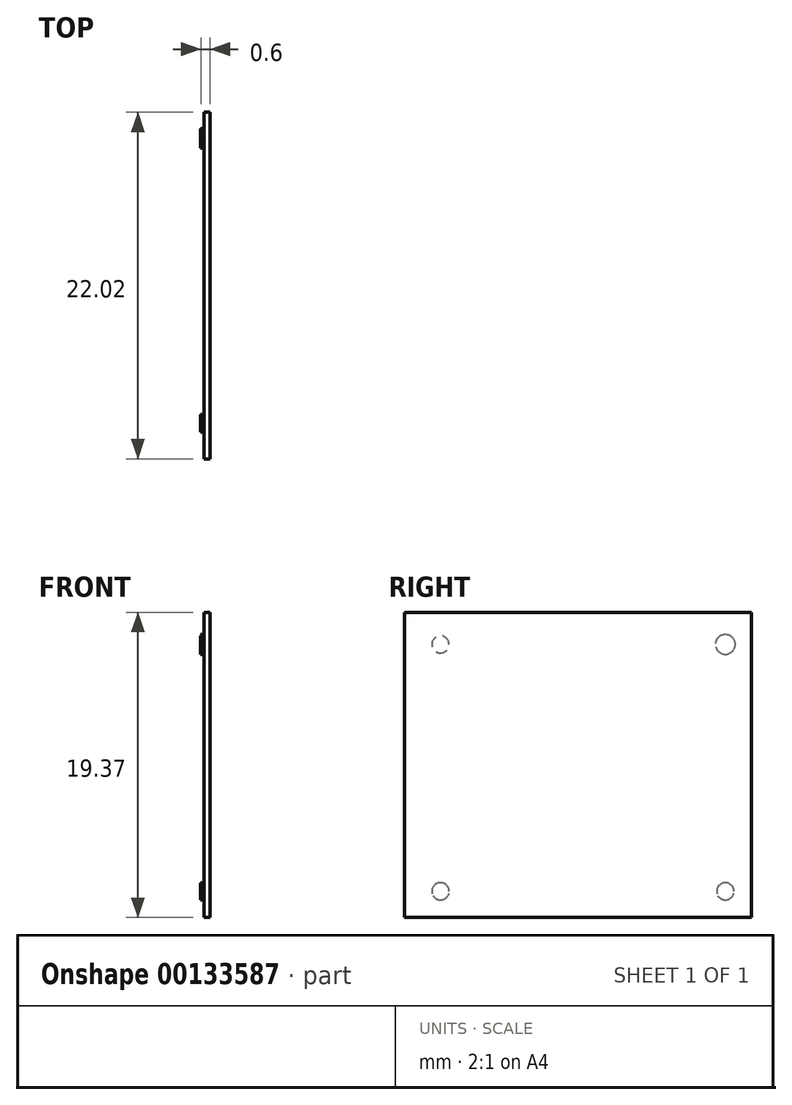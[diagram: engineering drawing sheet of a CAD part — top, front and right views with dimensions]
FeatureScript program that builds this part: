
annotation { "Feature Type Name" : "Feature", "Feature Type Description" : "" }
export const myFeature = defineFeature(function(context is Context, id is Id, definition is map)
    precondition{}
    {
        {
            var Q0;
            Q0=qCreatedBy(makeId("Right.planeOp"),FACE);
            var sketch = newSketch(context, id + "F0", { "sketchPlane" : qUnion([Q0])});
            skLineSegment(sketch, "E0.bottom", {"start": v(-14.75, 0) * mm, "end": v(7.27, 0) * mm});
            skLineSegment(sketch, "E0.top", {"start": v(-14.75, 19.37) * mm, "end": v(7.27, 19.37) * mm});
            skLineSegment(sketch, "E0.left", {"start": v(-14.75, 0) * mm, "end": v(-14.75, 19.37) * mm});
            skLineSegment(sketch, "E0.right", {"start": v(7.27, 0) * mm, "end": v(7.27, 19.37) * mm});
            skSolve(sketch);
        }
        {
            var Q0;
            Q0=makeQuery(id+"F0.imprint","IMPRINT",FACE,{"disambiguationData":[TD([[makeQuery(id+"F0.imprint","IMPRINT",EDGE,{"derivedFrom":sQuery(id+"F0.wireOp",EDGE,"E0.bottom")}),1.0]])]});
            extrude(context, id + "F1", {"entities" : qUnion([Q0]), "depth" : 0.38 * mm});
        }
        {
            var Q0;
            Q0=makeQuery(id+"F1.opExtrude","CAP_FACE",FACE,{"disambiguationData":[OSD([sQuery(id+"F0.wireOp",EDGE,"E0.bottom"),sQuery(id+"F0.wireOp",EDGE,"E0.top"),sQuery(id+"F0.wireOp",EDGE,"E0.left"),sQuery(id+"F0.wireOp",EDGE,"E0.right")])],"isStart":true});
            var sketch = newSketch(context, id + "F2", { "sketchPlane" : qUnion([Q0])});
            skCircle(sketch, "E1", {"center": v(12.48, 17.34) * mm, "radius": 0.55 * mm});
            skCircle(sketch, "E2", {"center": v(-5.61, 17.34) * mm, "radius": 0.63 * mm});
            skCircle(sketch, "E3", {"center": v(-5.61, 1.65) * mm, "radius": 0.55 * mm});
            skCircle(sketch, "E4", {"center": v(12.48, 1.65) * mm, "radius": 0.55 * mm});
            skSolve(sketch);
        }
        {
            var Q0;
            Q0=makeQuery(id+"F2.imprint","IMPRINT",FACE,{"disambiguationData":[TD([[makeQuery(id+"F2.imprint","IMPRINT",EDGE,{"derivedFrom":sQuery(id+"F2.wireOp",EDGE,"E1")}),1.0]])]});
            var Q1;
            Q1=makeQuery(id+"F2.imprint","IMPRINT",FACE,{"disambiguationData":[TD([[makeQuery(id+"F2.imprint","IMPRINT",EDGE,{"derivedFrom":sQuery(id+"F2.wireOp",EDGE,"E2")}),1.0]])]});
            var Q2;
            Q2=makeQuery(id+"F2.imprint","IMPRINT",FACE,{"disambiguationData":[TD([[makeQuery(id+"F2.imprint","IMPRINT",EDGE,{"derivedFrom":sQuery(id+"F2.wireOp",EDGE,"E3")}),1.0]])]});
            var Q3;
            Q3=makeQuery(id+"F2.imprint","IMPRINT",FACE,{"disambiguationData":[TD([[makeQuery(id+"F2.imprint","IMPRINT",EDGE,{"derivedFrom":sQuery(id+"F2.wireOp",EDGE,"E4")}),1.0]])]});
            extrude(context, id + "F3", {"entities" : qUnion([Q0, Q1, Q2, Q3]), "operationType" : NewBodyOperationType.ADD, "depth" : 0.22 * mm});
        }
    });
